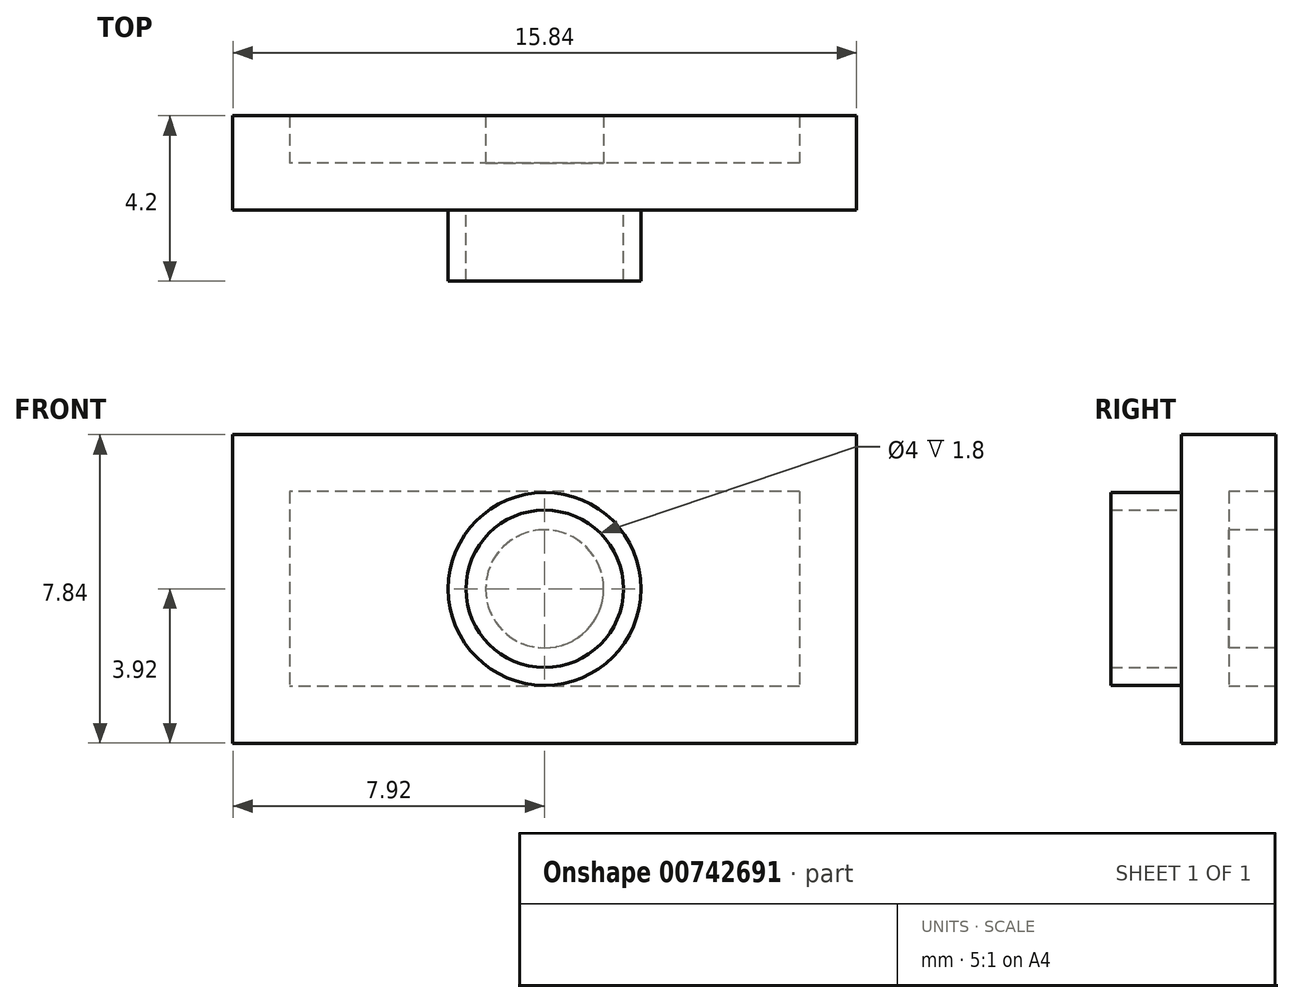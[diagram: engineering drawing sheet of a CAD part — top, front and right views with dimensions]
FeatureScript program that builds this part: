
annotation { "Feature Type Name" : "Feature", "Feature Type Description" : "" }
export const myFeature = defineFeature(function(context is Context, id is Id, definition is map)
    precondition{}
    {
        {
            var Q0;
            Q0=qCreatedBy(makeId("Front.planeOp"),FACE);
            var sketch = newSketch(context, id + "F0", { "sketchPlane" : qUnion([Q0])});
            skLineSegment(sketch, "E0.bottom", {"start": v(-7.92, 3.92) * mm, "end": v(7.93, 3.92) * mm});
            skLineSegment(sketch, "E0.top", {"start": v(-7.93, -3.92) * mm, "end": v(7.92, -3.92) * mm});
            skLineSegment(sketch, "E0.left", {"start": v(-7.92, 3.92) * mm, "end": v(-7.93, -3.92) * mm});
            skLineSegment(sketch, "E0.right", {"start": v(7.92, 3.92) * mm, "end": v(7.92, -3.92) * mm});
            skPoint(sketch, "E0.middle", {"position": v(0, 0) * mm});
            skSolve(sketch);
        }
        {
            var Q0;
            Q0 = qSketchRegion(id + "F0", true);
            extrude(context, id + "F1", {"entities" : qUnion([Q0]), "depth" : 1.2 * mm, "offsetDistance" : 25 * mm});
        }
        {
            var Q0;
            Q0=makeQuery(id+"F1.opExtrude","CAP_FACE",FACE,{"disambiguationData":[OSD([sQuery(id+"F0.wireOp",EDGE,"E0.bottom"),sQuery(id+"F0.wireOp",EDGE,"E0.top"),sQuery(id+"F0.wireOp",EDGE,"E0.left"),sQuery(id+"F0.wireOp",EDGE,"E0.right")])],"isStart":false});
            var sketch = newSketch(context, id + "F2", { "sketchPlane" : qUnion([Q0])});
            skCircle(sketch, "E1", {"center": v(0, 0) * mm, "radius": 2.45 * mm});
            skCircle(sketch, "E2", {"center": v(0, 0) * mm, "radius": 2 * mm});
            skSolve(sketch);
        }
        {
            var Q0;
            Q0 = qSketchRegion(id + "F2", true);
            extrude(context, id + "F3", {"entities" : qUnion([Q0]), "operationType" : NewBodyOperationType.ADD, "depth" : 1.8 * mm, "offsetDistance" : 25 * mm});
        }
        {
            var Q0;
            Q0=makeQuery(id+"F1.opExtrude","CAP_FACE",FACE,{"disambiguationData":[OSD([sQuery(id+"F0.wireOp",EDGE,"E0.bottom"),sQuery(id+"F0.wireOp",EDGE,"E0.top"),sQuery(id+"F0.wireOp",EDGE,"E0.left"),sQuery(id+"F0.wireOp",EDGE,"E0.right")])],"isStart":true});
            var sketch = newSketch(context, id + "F4", { "sketchPlane" : qUnion([Q0])});
            skLineSegment(sketch, "E3.bottom", {"start": v(-6.47, 2.47) * mm, "end": v(6.47, 2.47) * mm});
            skLineSegment(sketch, "E3.top", {"start": v(-6.47, -2.47) * mm, "end": v(6.47, -2.47) * mm});
            skLineSegment(sketch, "E3.left", {"start": v(-6.47, 2.47) * mm, "end": v(-6.47, -2.47) * mm});
            skLineSegment(sketch, "E3.right", {"start": v(6.47, 2.47) * mm, "end": v(6.47, -2.47) * mm});
            skPoint(sketch, "E3.middle", {"position": v(0, 0) * mm});
            skCircle(sketch, "E4", {"center": v(0, 0) * mm, "radius": 1.5 * mm});
            skSolve(sketch);
        }
        {
            var Q0;
            Q0=makeQuery(id+"F4.imprint","IMPRINT",FACE,{"disambiguationData":[TD([[makeQuery(id+"F4.imprint","IMPRINT",EDGE,{"derivedFrom":sQuery(id+"F4.wireOp",EDGE,"E3.bottom")}),1.0]])]});
            var Q1;
            Q1=makeQuery(id+"F4.imprint","IMPRINT",FACE,{"disambiguationData":[TD([[makeQuery(id+"F4.imprint","IMPRINT",EDGE,{"derivedFrom":sQuery(id+"F4.wireOp",EDGE,"E4")}),1.0]])]});
            extrude(context, id + "F5", {"entities" : qUnion([Q0, Q1]), "operationType" : NewBodyOperationType.ADD, "depth" : 1.2 * mm, "offsetDistance" : 25 * mm});
        }
    });
